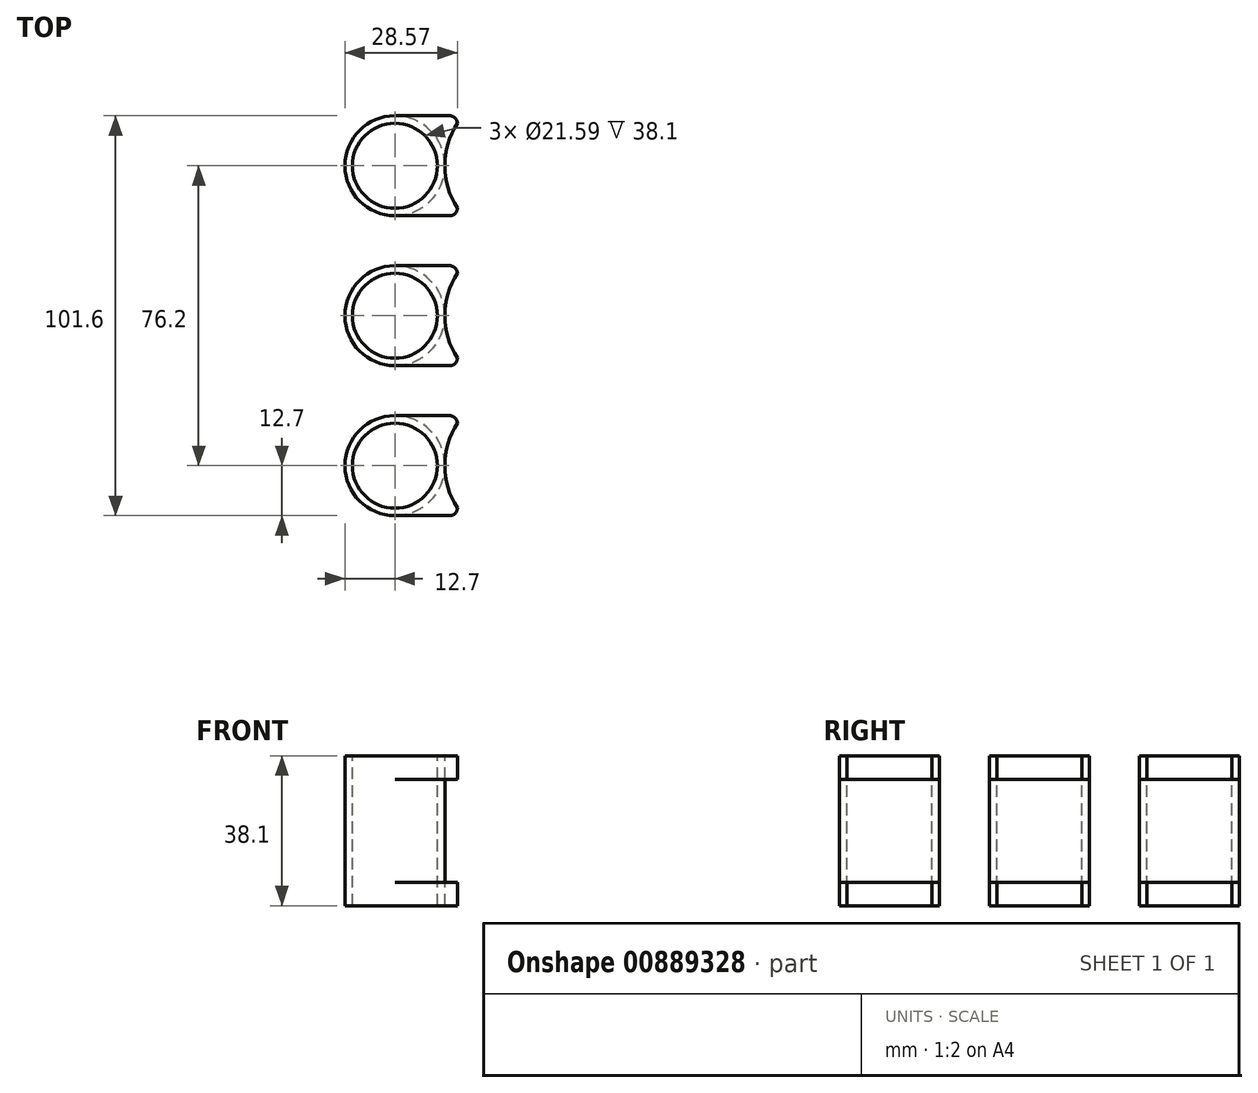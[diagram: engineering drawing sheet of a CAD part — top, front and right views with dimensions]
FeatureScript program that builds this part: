
annotation { "Feature Type Name" : "Feature", "Feature Type Description" : "" }
export const myFeature = defineFeature(function(context is Context, id is Id, definition is map)
    precondition{}
    {
        {
            var Q0;
            Q0=qCreatedBy(makeId("Top.planeOp"),FACE);
            var sketch = newSketch(context, id + "F0", { "sketchPlane" : qUnion([Q0])});
            skCircle(sketch, "E0", {"center": v(0, 0) * mm, "radius": 12.7 * mm});
            skCircle(sketch, "E1", {"center": v(0, 0) * mm, "radius": 10.8 * mm});
            skSolve(sketch);
        }
        {
            var Q0;
            Q0=qCreatedBy(makeId("Top.planeOp"),FACE);
            var sketch = newSketch(context, id + "F1", { "sketchPlane" : qUnion([Q0])});
            skLineSegment(sketch, "E2", {"start": v(0, -12.7) * mm, "end": v(13.97, -12.7) * mm});
            skLineSegment(sketch, "E3", {"start": v(15.87, -10.8) * mm, "end": v(15.87, 10.8) * mm});
            skLineSegment(sketch, "E4", {"start": v(13.97, 12.7) * mm, "end": v(0, 12.7) * mm});
            skCircle(sketch, "E5", {"center": v(13.97, -10.8) * mm, "radius": 1.9 * mm});
            skLineSegment(sketch, "E6", {"start": v(0, 0) * mm, "end": v(13.97, -10.8) * mm});
            skCircle(sketch, "E7.MirrorC", {"center": v(13.97, 10.8) * mm, "radius": 1.9 * mm});
            skPoint(sketch, "E8.MirrorCS.end.orphan", {"position": v(13.97, 8.9) * mm});
            skPoint(sketch, "E8.MirrorCS.start.orphan", {"position": v(15.87, 8.9) * mm});
            skPoint(sketch, "E9.end.orphan", {"position": v(13.97, -8.9) * mm});
            skPoint(sketch, "E9.start.orphan", {"position": v(15.87, -8.9) * mm});
            skArc(sketch, "E10", {"start": v(0, -12.7) * mm, "mid": v(12.7, 0) * mm, "end": v(0, 12.7) * mm});
            skSolve(sketch);
        }
        {
            var Q0;
            Q0=makeQuery(id+"F0.imprint","IMPRINT",FACE,{"disambiguationData":[TD([[makeQuery(id+"F0.imprint","IMPRINT",EDGE,{"derivedFrom":sQuery(id+"F0.wireOp",EDGE,"E0")}),1.0]])]});
            var Q1;
            {var subQ0=sQuery(id+"F1.wireOp",EDGE,"E7.MirrorC");var subQ1=makeQuery(id+"F1.imprint","INTERSECT",VERTEX,{"derivedFrom":[sQuery(id+"F1.wireOp",EDGE,"E3"),subQ0]});Q1=makeQuery(id+"F1.imprint","IMPRINT",FACE,{"disambiguationData":[TD([[makeQuery(id+"F1.imprint","IMPRINT",EDGE,{"disambiguationData":[TD([[subQ1,-1.0]])],"derivedFrom":subQ0}),-1.0]])]});}
            var Q2;
            {var subQ0=sQuery(id+"F1.wireOp",EDGE,"E5");var subQ1=makeQuery(id+"F1.imprint","INTERSECT",VERTEX,{"derivedFrom":[sQuery(id+"F1.wireOp",EDGE,"E2"),subQ0]});Q2=makeQuery(id+"F1.imprint","IMPRINT",FACE,{"disambiguationData":[TD([[makeQuery(id+"F1.imprint","IMPRINT",EDGE,{"disambiguationData":[TD([[subQ1,-1.0]])],"derivedFrom":subQ0}),-1.0]])]});}
            extrude(context, id + "F2", {"entities" : qUnion([Q0, Q1, Q2]), "depth" : 13.08 * mm, "offsetDistance" : 25.4 * mm});
        }
        {
            var Q0;
            Q0=qSketchRegion(id+"F0",true);
            var Q1;
            Q1=qSketchRegion(id+"F1",true);
            var Q2;
            Q2=makeQuery(id+"F2.opExtrude","CAP_FACE",FACE,{"disambiguationData":[OSD([sQuery(id+"F1.wireOp",EDGE,"E7.MirrorC")])],"isStart":true});
            var Q3;
            Q3=makeQuery(id+"F2.opExtrude","CAP_FACE",FACE,{"disambiguationData":[OSD([sQuery(id+"F0.wireOp",EDGE,"E0"),sQuery(id+"F0.wireOp",EDGE,"E1")])],"isStart":true});
            var Q4;
            Q4=makeQuery(id+"F2.opExtrude","CAP_FACE",FACE,{"disambiguationData":[OSD([sQuery(id+"F1.wireOp",EDGE,"E5")])],"isStart":true});
            extrude(context, id + "F3", {"entities" : qUnion([Q0, Q1, Q2, Q3, Q4]), "oppositeDirection" : true, "depth" : 5.97 * mm, "offsetDistance" : 25.4 * mm});
        }
        {
            var Q0;
            Q0=makeQuery(id+"F2.opExtrude","CAP_FACE",FACE,{"disambiguationData":[OSD([sQuery(id+"F0.wireOp",EDGE,"E0"),sQuery(id+"F0.wireOp",EDGE,"E1")])],"isStart":false});
            cPlane(context, id + "F4", {"entities" : qUnion([Q0]), "cplaneType" : CPlaneType.OFFSET, "offset" : 0 * mm, "width" : 152.4 * mm, "height" : 152.4 * mm});
        }
        {
            var Q0;
            Q0=makeQuery(id+"F3.opExtrude","SWEPT_BODY",BODY,{"disambiguationData":[OSD([sQuery(id+"F1.wireOp",EDGE,"E2"),sQuery(id+"F1.wireOp",EDGE,"E3"),sQuery(id+"F1.wireOp",EDGE,"E4"),sQuery(id+"F1.wireOp",EDGE,"E5"),sQuery(id+"F1.wireOp",EDGE,"E7.MirrorC"),sQuery(id+"F1.wireOp",EDGE,"E10")])]});
            var Q1;
            Q1=makeQuery(id+"F2.opExtrude","SWEPT_BODY",BODY,{"disambiguationData":[OSD([sQuery(id+"F1.wireOp",EDGE,"E5")])]});
            var Q2;
            Q2=makeQuery(id+"F2.opExtrude","SWEPT_BODY",BODY,{"disambiguationData":[OSD([sQuery(id+"F1.wireOp",EDGE,"E7.MirrorC")])]});
            var Q3;
            Q3=makeQuery(id+"F3.opExtrude","SWEPT_BODY",BODY,{"disambiguationData":[OSD([sQuery(id+"F1.wireOp",EDGE,"E5")])]});
            var Q4;
            Q4=makeQuery(id+"F3.opExtrude","SWEPT_BODY",BODY,{"disambiguationData":[OSD([sQuery(id+"F1.wireOp",EDGE,"E7.MirrorC")])]});
            var Q5;
            {var subQ0=sQuery(id+"F0.wireOp",EDGE,"E1");var subQ1=sQuery(id+"F0.wireOp",EDGE,"E0");Q5=makeQuery(id+"F3.opExtrude","SWEPT_BODY",BODY,{"disambiguationData":[OSD([subQ1,subQ0]),TDD([makeQuery(id+"F0.imprint","IMPRINT",EDGE,{"derivedFrom":subQ1}),makeQuery(id+"F0.imprint","IMPRINT",EDGE,{"derivedFrom":subQ0})])]});}
            var Q6;
            Q6=makeQuery(id+"F2.opExtrude","SWEPT_BODY",BODY,{"disambiguationData":[OSD([sQuery(id+"F0.wireOp",EDGE,"E0"),sQuery(id+"F0.wireOp",EDGE,"E1")])]});
            booleanBodies(context, id + "F5", {"operationType" : BooleanOperationType.UNION, "tools" : qUnion([Q0, Q1, Q2, Q3, Q4, Q5, Q6])});
        }
        {
            var Q0;
            {var subQ0=sQuery(id+"F0.wireOp",EDGE,"E1");var subQ1=sQuery(id+"F0.wireOp",EDGE,"E0");Q0=makeQuery(id+"F3.opExtrude","SWEPT_BODY",BODY,{"disambiguationData":[OSD([subQ1,subQ0]),TDD([makeQuery(id+"F2.opExtrude","CAP_FACE",FACE,{"disambiguationData":[OSD([subQ1,subQ0])],"isStart":true})])]});}
            var Q1;
            Q1=makeQuery(id+"F3.opExtrude","SWEPT_BODY",BODY,{"disambiguationData":[OSD([sQuery(id+"F1.wireOp",EDGE,"E2"),sQuery(id+"F1.wireOp",EDGE,"E3"),sQuery(id+"F1.wireOp",EDGE,"E4"),sQuery(id+"F1.wireOp",EDGE,"E5"),sQuery(id+"F1.wireOp",EDGE,"E7.MirrorC"),sQuery(id+"F1.wireOp",EDGE,"E10")])]});
            booleanBodies(context, id + "F6", {"operationType" : BooleanOperationType.UNION, "tools" : qUnion([Q0, Q1])});
        }
        {
            var Q0;
            {var subQ0=sQuery(id+"F0.wireOp",EDGE,"E1");var subQ1=sQuery(id+"F0.wireOp",EDGE,"E0");Q0=makeQuery(id+"F3.opExtrude","SWEPT_BODY",BODY,{"disambiguationData":[OSD([subQ1,subQ0]),TDD([makeQuery(id+"F2.opExtrude","CAP_FACE",FACE,{"disambiguationData":[OSD([subQ1,subQ0])],"isStart":true})])]});}
            var Q1;
            Q1=qCreatedBy(id+"F4.planeOp",FACE);
            mirror(context, id + "F7", {"operationType" : NewBodyOperationType.ADD, "entities" : qUnion([Q0]), "mirrorPlane" : qUnion([Q1])});
        }
        {
            var Q0;
            {var subQ0=sQuery(id+"F0.wireOp",EDGE,"E1");var subQ1=sQuery(id+"F0.wireOp",EDGE,"E0");Q0=makeQuery(id+"F7.opPattern","COPY",FACE,{"derivedFrom":makeQuery(id+"F6.opBoolean","MERGE",FACE,{"derivedFrom":[makeQuery(id+"F3.opExtrude","CAP_FACE",FACE,{"disambiguationData":[OSD([subQ1,subQ0]),TDD([makeQuery(id+"F2.opExtrude","CAP_FACE",FACE,{"disambiguationData":[OSD([subQ1,subQ0])],"isStart":true})])],"isStart":false}),makeQuery(id+"F5.opBoolean","MERGE",FACE,{"derivedFrom":[makeQuery(id+"F3.opExtrude","CAP_FACE",FACE,{"disambiguationData":[OSD([subQ1,subQ0]),TDD([makeQuery(id+"F0.imprint","IMPRINT",EDGE,{"derivedFrom":subQ1}),makeQuery(id+"F0.imprint","IMPRINT",EDGE,{"derivedFrom":subQ0})])],"isStart":false}),makeQuery(id+"F3.opExtrude","CAP_FACE",FACE,{"disambiguationData":[OSD([sQuery(id+"F1.wireOp",EDGE,"E2"),sQuery(id+"F1.wireOp",EDGE,"E3"),sQuery(id+"F1.wireOp",EDGE,"E4"),sQuery(id+"F1.wireOp",EDGE,"E5"),sQuery(id+"F1.wireOp",EDGE,"E7.MirrorC"),sQuery(id+"F1.wireOp",EDGE,"E10")])],"isStart":false})]})]}),"instanceName":"1"});}
            var sketch = newSketch(context, id + "F8", { "sketchPlane" : qUnion([Q0])});
            skArc(sketch, "E11", {"start": v(15.87, 10.8) * mm, "mid": v(12.7, 0) * mm, "end": v(15.87, -10.8) * mm});
            skLineSegment(sketch, "E12", {"start": v(0, 0) * mm, "end": v(12.7, 0) * mm});
            skPoint(sketch, "E12.endSnap0", {"position": v(12.7, 0) * mm});
            skSolve(sketch);
        }
        {
            var Q0;
            {var subQ2=sQuery(id+"F1.wireOp",EDGE,"E3");var subQ3=makeQuery(id+"F7.opPattern","COPY",EDGE,{"derivedFrom":makeQuery(id+"F3.opExtrude","CAP_EDGE",EDGE,{"disambiguationData":[OSD([subQ2])],"isStart":false}),"instanceName":"1"});Q0=makeQuery(id+"F8.imprint","IMPRINT",FACE,{"disambiguationData":[TD([[makeQuery(id+"F8.imprint","IMPRINT",EDGE,{"derivedFrom":subQ3}),1.0]])]});}
            extrude(context, id + "F9", {"entities" : qUnion([Q0]), "operationType" : NewBodyOperationType.REMOVE, "oppositeDirection" : true, "depth" : 37.34 * mm, "offsetDistance" : 25.4 * mm});
        }
        {
            var Q0;
            Q0=makeQuery(id+"F9.boolean.opBoolean","COPY",FACE,{"derivedFrom":makeQuery(id+"F9.opExtrude","CAP_FACE",FACE,{"disambiguationData":[OSD([sQuery(id+"F1.wireOp",EDGE,"E3"),sQuery(id+"F8.wireOp",EDGE,"E11")])],"isStart":false})});
            extrude(context, id + "F10", {"entities" : qUnion([Q0]), "operationType" : NewBodyOperationType.REMOVE, "oppositeDirection" : true, "depth" : 1.27 * mm, "offsetDistance" : 25.4 * mm});
        }
        {
            var Q0;
            {var subQ0=sQuery(id+"F0.wireOp",EDGE,"E1");var subQ1=sQuery(id+"F0.wireOp",EDGE,"E0");Q0=makeQuery(id+"F3.opExtrude","SWEPT_BODY",BODY,{"disambiguationData":[OSD([subQ1,subQ0]),TDD([makeQuery(id+"F2.opExtrude","CAP_FACE",FACE,{"disambiguationData":[OSD([subQ1,subQ0])],"isStart":true})])]});}
            transform(context, id + "F11", {"entities" : qUnion([Q0]), "transformType" : TransformType.TRANSLATION_3D, "dx" : 0 * mm, "dy" : 38.1 * mm, "dz" : 0 * mm, "makeCopy" : true});
        }
        {
            var Q0;
            {var subQ0=sQuery(id+"F0.wireOp",EDGE,"E1");var subQ1=sQuery(id+"F0.wireOp",EDGE,"E0");Q0=makeQuery(id+"F3.opExtrude","SWEPT_BODY",BODY,{"disambiguationData":[OSD([subQ1,subQ0]),TDD([makeQuery(id+"F2.opExtrude","CAP_FACE",FACE,{"disambiguationData":[OSD([subQ1,subQ0])],"isStart":true})])]});}
            transform(context, id + "F12", {"entities" : qUnion([Q0]), "transformType" : TransformType.TRANSLATION_3D, "dx" : 0 * mm, "dy" : -38.1 * mm, "dz" : 0 * mm, "makeCopy" : true});
        }
    });
